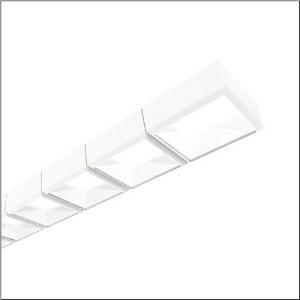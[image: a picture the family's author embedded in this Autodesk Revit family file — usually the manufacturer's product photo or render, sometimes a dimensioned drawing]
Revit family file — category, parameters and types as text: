
# Revit family: scriptus_r__11_5mz312d0twb_510a
name_source: partatom
category: Lighting Fixtures
units: mm (PartAtom-declared; Revit-internal decimal feet)

## family parameters
Cut with Voids When Loaded = No
Host = Face
Light Source = No
Part Type = Normal
Room Calculation Point = No
Round Connector Dimension = Use Diameter
Shared = No

## types (1)
- --- (1 x LED 3000K+6500K / CRI = 80 (unbekannt), 3200 lm / 2380 lm, 3000K)
    Apparent Load = 94 VA
    CIE Flux Codes = 0 0 0 0 100 / 82 95 99 100 100
    Color Rendering = 80
    Color Temperature = 3000K
    Default Elevation = 1800 mm
    Description = Scriptus® 11, office luminaire, primary optical cover: lenses, CAT 2 (L<= 3000cd/m²), light emission: direct/indirect distribution, primary light characteristic: symmetric, installation type: suspended mounting, LED rated luminous flux: 11.150 lm, light colour: 8tw, colour temperature: 3000..6500K, control gear: ECG DALI, with terminal, 5-pole, mains connection: 230V, AC, 50Hz, rated input power: 96W, LED control gear: ECG DALI, housing, luminaire housing, of aluminium, traffic white (RAL 9016), length: 1.768 mm, width: 114 mm, height: 57mm, protection rating (complete): IP20, insulation class (complete): insulation class I (protective earthing), certification: CE, protection symbol: F, permissible ambient temperature for indoor applications: <= +25°C, standard: EN 50419, packaging unit: 1 piece
    Height = 57 mm
    Lamp = 1 x LED 3000K+6500K / CRI >= 80 (unbekannt)
    Lamp Light Flux = 3200 lm / 2380 lm
    Lamp count = 1
    Length = 1768 mm
    Luminous efficacy = 119 lm/W
    Manufacturer = Siteco
    ModVariant = No
    Model = 5MZ312D0TWB
    Mounting Place = Ceiling
    Mounting Type = Pendant
    Number of Poles = 1
    OnlyDefault = Yes
    Power Factor = 1
    Product Name = Scriptus® 11
    Product group = office luminaire | ceiling pendant
    ProductGroupID = 905
    Protection Class = Protection class I
    Protection Degree = IP 20
    RLX_Detail_Level = 1
    RlxData = <blob elided: 31653 chars, md5=2a53efa7>
    Socket = socket
    Standby Power = 0 W
    System Light Flux = 11160 lm
    System Power = 94 W
    Type Comments = individual setting: colour temperature 6500K
    Type Image = l_1004839.jpg
    URL = http://relux.com
    VarID = @adj_146268
    Voltage = 0 V
    Weight = 0.00 kg
    Width = 114 mm

## geometry (parser evidence)
native form markers: Blend x4, Sweep x19
no freeform markers — native parametric forms only
